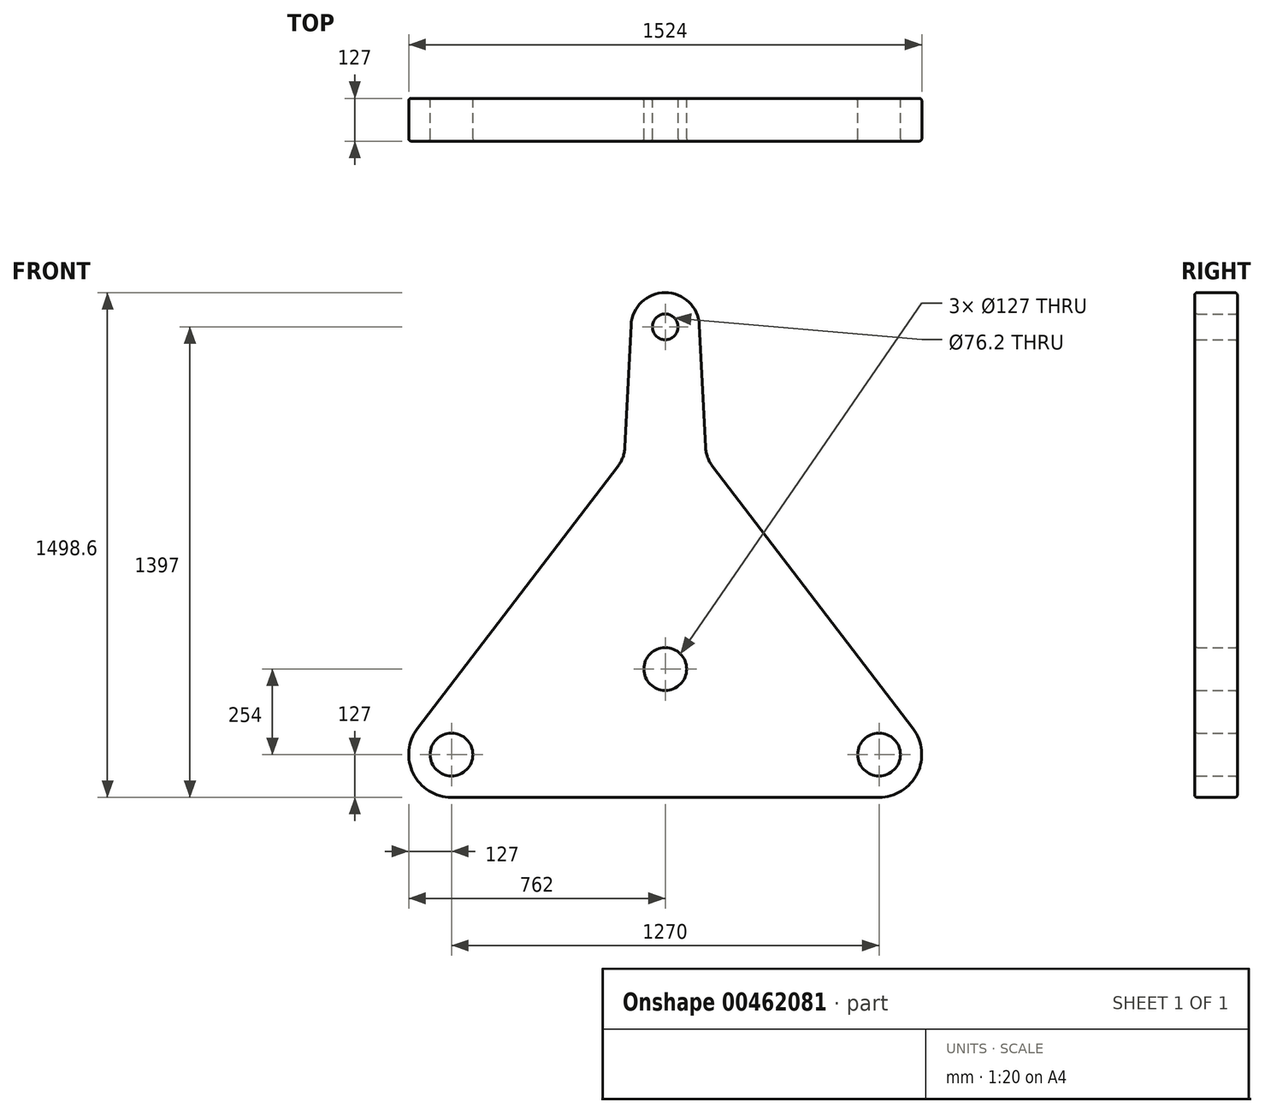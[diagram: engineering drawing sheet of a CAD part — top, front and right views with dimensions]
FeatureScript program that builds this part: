
annotation { "Feature Type Name" : "Feature", "Feature Type Description" : "" }
export const myFeature = defineFeature(function(context is Context, id is Id, definition is map)
    precondition{}
    {
        {
            var Q0;
            Q0=qCreatedBy(makeId("Front.planeOp"),FACE);
            var sketch = newSketch(context, id + "F0", { "sketchPlane" : qUnion([Q0])});
            skCircle(sketch, "E0", {"center": v(0, -627.26) * mm, "radius": 63.5 * mm});
            skCircle(sketch, "E1", {"center": v(0, 388.74) * mm, "radius": 38.1 * mm});
            skArc(sketch, "E2", {"start": v(101.47, 393.82) * mm, "mid": v(0, 490.34) * mm, "end": v(-101.47, 393.82) * mm});
            skLineSegment(sketch, "E3", {"start": v(-101.47, 393.82) * mm, "end": v(-119.6, 31.54) * mm});
            skLineSegment(sketch, "E4", {"start": v(101.47, 393.82) * mm, "end": v(119.6, 31.54) * mm});
            skCircle(sketch, "E5", {"center": v(635, -881.26) * mm, "radius": 63.5 * mm});
            skCircle(sketch, "E6", {"center": v(-635, -881.26) * mm, "radius": 63.5 * mm});
            skArc(sketch, "E7", {"start": v(-735.9, -804.13) * mm, "mid": v(-748.85, -937.53) * mm, "end": v(-635, -1008.26) * mm});
            skArc(sketch, "E8", {"start": v(635, -1008.26) * mm, "mid": v(748.85, -937.53) * mm, "end": v(735.9, -804.13) * mm});
            skLineSegment(sketch, "E9", {"start": v(-735.9, -804.13) * mm, "end": v(-140.37, -25.09) * mm});
            skLineSegment(sketch, "E10", {"start": v(140.37, -25.09) * mm, "end": v(735.9, -804.13) * mm});
            skLineSegment(sketch, "E11", {"start": v(-635, -1008.26) * mm, "end": v(635, -1008.26) * mm});
            skPoint(sketch, "E12.visualSharp", {"position": v(-121.19, 0) * mm});
            skArc(sketch, "E12.filletArc", {"start": v(-140.37, -25.09) * mm, "mid": v(-125.69, 1.65) * mm, "end": v(-119.6, 31.54) * mm});
            skPoint(sketch, "E13.visualSharp", {"position": v(121.19, 0) * mm});
            skArc(sketch, "E13.filletArc", {"start": v(119.6, 31.54) * mm, "mid": v(125.69, 1.65) * mm, "end": v(140.37, -25.09) * mm});
            skSolve(sketch);
        }
        {
            var Q0;
            Q0=makeQuery(id+"F0.imprint","IMPRINT",FACE,{"disambiguationData":[TD([[makeQuery(id+"F0.imprint","IMPRINT",EDGE,{"derivedFrom":sQuery(id+"F0.wireOp",EDGE,"E0")}),-1.0]])]});
            extrude(context, id + "F1", {"entities" : qUnion([Q0]), "endBound" : BoundingType.SYMMETRIC, "depth" : 127 * mm});
        }
        {
            var Q0;
            Q0=makeQuery(id+"F1.opExtrude","CAP_EDGE",EDGE,{"disambiguationData":[OSD([sQuery(id+"F0.wireOp",EDGE,"E2")])],"isStart":false});
            var Q1;
            Q1=makeQuery(id+"F1.opExtrude","CAP_EDGE",EDGE,{"disambiguationData":[OSD([sQuery(id+"F0.wireOp",EDGE,"E4")])],"isStart":false});
            var Q2;
            Q2=makeQuery(id+"F1.opExtrude","CAP_EDGE",EDGE,{"disambiguationData":[OSD([sQuery(id+"F0.wireOp",EDGE,"E3")])],"isStart":false});
            var Q3;
            Q3=makeQuery(id+"F1.opExtrude","CAP_EDGE",EDGE,{"disambiguationData":[OSD([sQuery(id+"F0.wireOp",EDGE,"E10")])],"isStart":true});
            var Q4;
            Q4=makeQuery(id+"F1.opExtrude","CAP_EDGE",EDGE,{"disambiguationData":[OSD([sQuery(id+"F0.wireOp",EDGE,"E13.filletArc")])],"isStart":true});
            var Q5;
            Q5=makeQuery(id+"F1.opExtrude","CAP_EDGE",EDGE,{"disambiguationData":[OSD([sQuery(id+"F0.wireOp",EDGE,"E4")])],"isStart":true});
            var Q6;
            Q6=makeQuery(id+"F1.opExtrude","CAP_EDGE",EDGE,{"disambiguationData":[OSD([sQuery(id+"F0.wireOp",EDGE,"E11")])],"isStart":false});
            var Q7;
            Q7=makeQuery(id+"F1.opExtrude","CAP_EDGE",EDGE,{"disambiguationData":[OSD([sQuery(id+"F0.wireOp",EDGE,"E6")])],"isStart":false});
            var Q8;
            Q8=makeQuery(id+"F1.opExtrude","CAP_EDGE",EDGE,{"disambiguationData":[OSD([sQuery(id+"F0.wireOp",EDGE,"E6")])],"isStart":true});
            var Q9;
            Q9=makeQuery(id+"F1.opExtrude","CAP_EDGE",EDGE,{"disambiguationData":[OSD([sQuery(id+"F0.wireOp",EDGE,"E0")])],"isStart":true});
            var Q10;
            Q10=makeQuery(id+"F1.opExtrude","CAP_EDGE",EDGE,{"disambiguationData":[OSD([sQuery(id+"F0.wireOp",EDGE,"E0")])],"isStart":false});
            var Q11;
            Q11=makeQuery(id+"F1.opExtrude","CAP_EDGE",EDGE,{"disambiguationData":[OSD([sQuery(id+"F0.wireOp",EDGE,"E5")])],"isStart":false});
            var Q12;
            Q12=makeQuery(id+"F1.opExtrude","CAP_EDGE",EDGE,{"disambiguationData":[OSD([sQuery(id+"F0.wireOp",EDGE,"E5")])],"isStart":true});
            var Q13;
            Q13=makeQuery(id+"F1.opExtrude","CAP_EDGE",EDGE,{"disambiguationData":[OSD([sQuery(id+"F0.wireOp",EDGE,"E1")])],"isStart":false});
            var Q14;
            Q14=makeQuery(id+"F1.opExtrude","CAP_EDGE",EDGE,{"disambiguationData":[OSD([sQuery(id+"F0.wireOp",EDGE,"E1")])],"isStart":true});
            fillet(context, id + "F2", {"entities" : qUnion([Q0, Q1, Q2, Q3, Q4, Q5, Q6, Q7, Q8, Q9, Q10, Q11, Q12, Q13, Q14]), "radius" : 7.62 * mm, "tangentPropagation" : true, "allowEdgeOverflow" : false});
        }
    });
